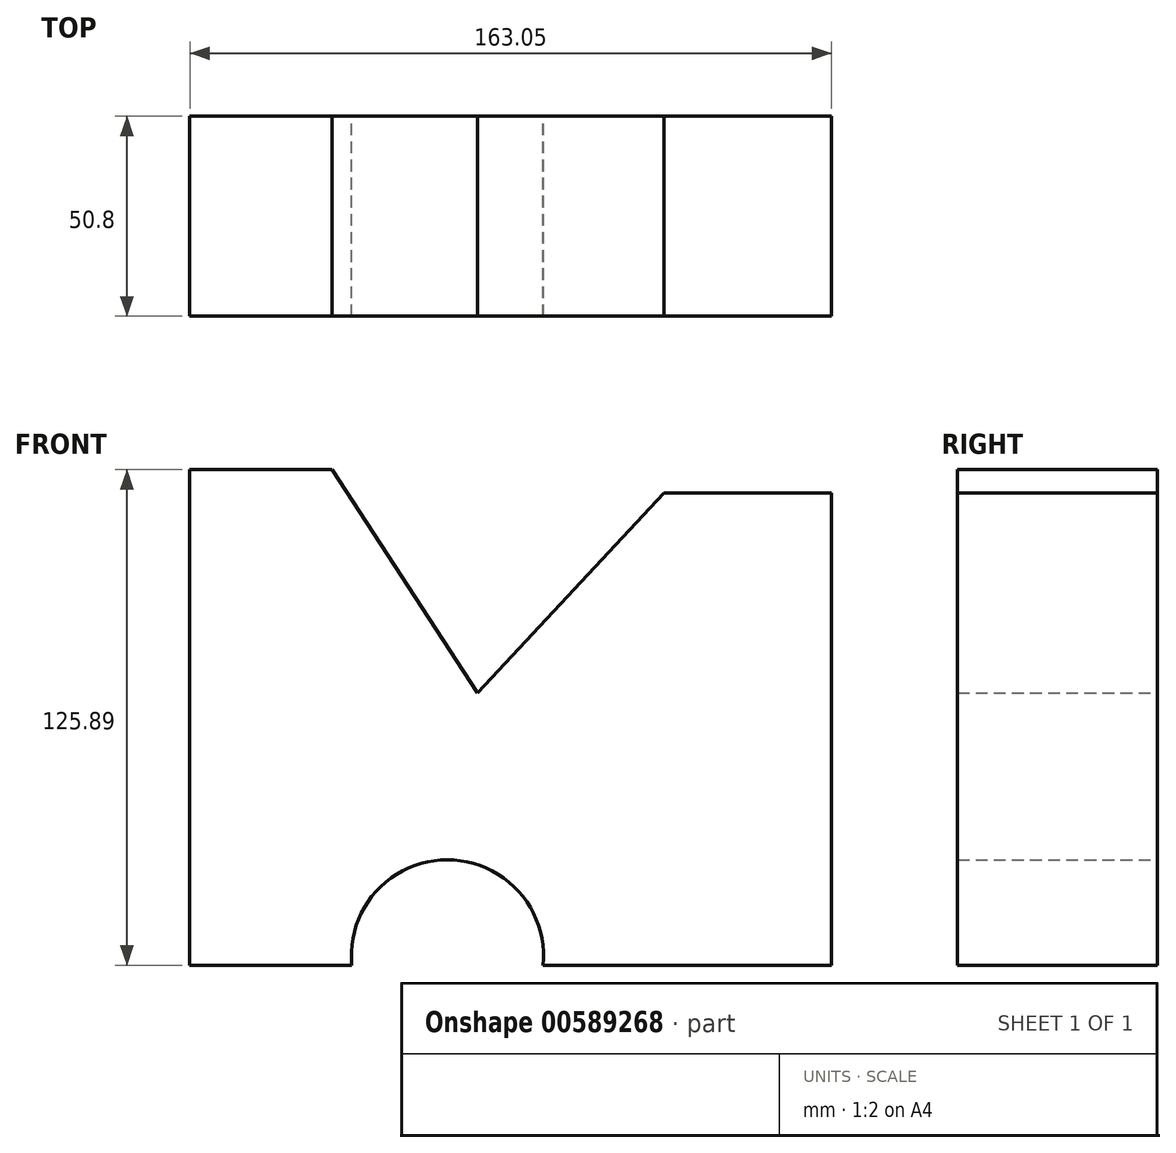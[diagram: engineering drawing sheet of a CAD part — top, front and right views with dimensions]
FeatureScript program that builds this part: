
annotation { "Feature Type Name" : "Feature", "Feature Type Description" : "" }
export const myFeature = defineFeature(function(context is Context, id is Id, definition is map)
    precondition{}
    {
        {
            var Q0;
            Q0=qCreatedBy(makeId("Front.planeOp"),FACE);
            var sketch = newSketch(context, id + "F0", { "sketchPlane" : qUnion([Q0])});
            skLineSegment(sketch, "E0", {"start": v(0, 0) * mm, "end": v(47.33, 50.8) * mm});
            skLineSegment(sketch, "E1", {"start": v(47.33, 50.8) * mm, "end": v(89.95, 50.8) * mm});
            skLineSegment(sketch, "E2", {"start": v(89.95, 50.8) * mm, "end": v(89.95, -69.14) * mm});
            skLineSegment(sketch, "E3", {"start": v(89.95, -69.14) * mm, "end": v(16.6, -69.14) * mm});
            skArc(sketch, "E4", {"start": v(16.6, -69.14) * mm, "mid": v(-7.68, -42.36) * mm, "end": v(-31.97, -69.14) * mm});
            skLineSegment(sketch, "E5", {"start": v(-31.97, -69.14) * mm, "end": v(-73.1, -69.14) * mm});
            skLineSegment(sketch, "E6", {"start": v(-73.1, -69.14) * mm, "end": v(-73.1, 56.75) * mm});
            skLineSegment(sketch, "E7", {"start": v(-73.1, 56.75) * mm, "end": v(-36.92, 56.75) * mm});
            skLineSegment(sketch, "E8", {"start": v(-36.92, 56.75) * mm, "end": v(0, 0) * mm});
            skSolve(sketch);
        }
        {
            var Q0;
            Q0=makeQuery(id+"F0.imprint","IMPRINT",FACE,{"disambiguationData":[TD([[makeQuery(id+"F0.imprint","IMPRINT",EDGE,{"derivedFrom":sQuery(id+"F0.wireOp",EDGE,"E0")}),-1.0]])]});
            extrude(context, id + "F1", {"entities" : qUnion([Q0]), "depth" : 50.8 * mm, "offsetDistance" : 25.4 * mm});
        }
    });
